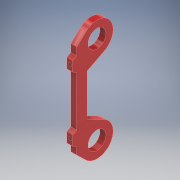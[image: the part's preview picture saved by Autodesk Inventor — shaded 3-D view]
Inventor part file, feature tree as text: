
AUTODESK INVENTOR PART (.ipt)
format: ipt  version: 2022 (Build 260153000, 153)  size: 143,360 bytes
history: native  units: mm
features: sketch x2, hole x2, extrude x1, plane x1
ambient origin geometry x8: Origin, YZ Plane, XZ Plane, XY Plane, X Axis, Y Axis, Z Axis, Center Point
bodies: Body1 (feature_tree)
feature tree (6):
  sketch  "Sketch1"  dims[d23=12.0mm d24=0.0mm]
  extrude  "Extrusion2"  [1 undecoded]
  hole  "Hole4"  [1 undecoded]
  plane  "Work Plane2"
  hole  "Hole5"  [1 undecoded]
  sketch  "Sketch3"  dims[d25=36.0mm d26=6.0mm d27=4.0mm d28=2.0mm d29=90.0deg d30=8.0mm d31=20.594885mm d32=6.647mm d33=16.0mm d34=4.0mm d35=2.0mm d36=90.0deg d37=20.0mm d38=20.594885mm]
note: 3 required parameter values undecoded (feature->parameter linkage not recoverable at this tier; creation-order binding heuristic only, values carry confidence <= 0.55)
